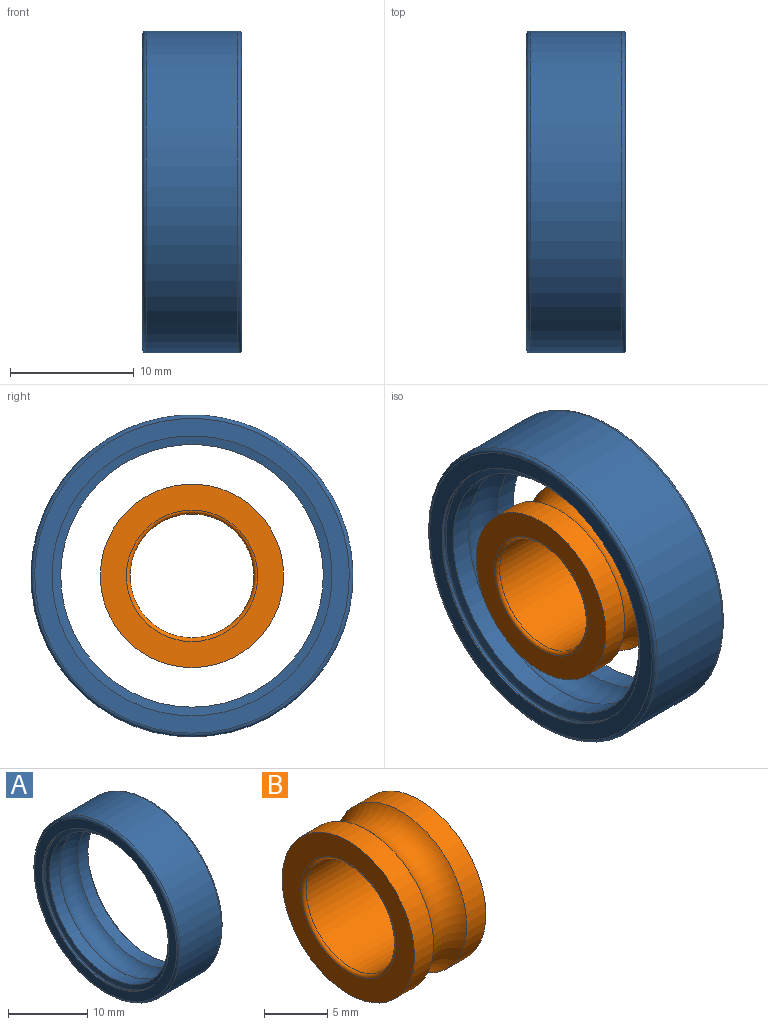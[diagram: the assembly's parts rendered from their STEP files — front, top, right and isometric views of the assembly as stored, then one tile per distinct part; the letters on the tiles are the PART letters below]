
ASSEMBLY  parts=2 mates=1
PART A: 14 faces, bbox 8x28.1x28.1 mm
  f0: plane 25.4x25.4mm, normal (-1,0,0), area 105.6mm2, adj f1,f13
  f1: cylinder r=11.3mm len=22.6mm, axis (-1,0,0), area 6.4mm2, adj f0,f2
  f2: torus R=11.3mm, axis (1,0,0), area 40.6mm2, adj f1,f3
  f3: cone r=11.3mm half-angle=80deg, axis (-1,0,0), area 48.9mm2, adj f2,f4
  f4: cylinder r=10.6mm len=21.2mm, axis (-1,0,0), area 117.2mm2, adj f3,f5
  f5: torus R=8.9mm, axis (1,0,0), area 256.4mm2, adj f4,f6
  f6: cylinder r=10.6mm len=21.2mm, axis (-1,0,0), area 117.2mm2, adj f5,f7
  f7: cone r=10.6mm half-angle=80deg, axis (1,0,0), area 48.9mm2, adj f6,f8
  f8: torus R=11.3mm, axis (1,0,0), area 40.6mm2, adj f7,f9
  f9: cylinder r=11.3mm len=22.6mm, axis (-1,0,0), area 6.4mm2, adj f8,f10
  f10: plane 25.4x25.4mm, normal (1,0,0), area 105.6mm2, adj f9,f11
  f11: torus R=12.7mm, axis (1,0,0), area 38.2mm2, adj f10,f12
  f12: cylinder r=13mm len=26mm, axis (-1,0,0), area 604.4mm2, adj f11,f13
  f13: torus R=12.7mm, axis (1,0,0), area 38.2mm2, adj f0,f12
PART B: 8 faces, bbox 8x19.3x19.3 mm
  f0: plane 14.8x14.8mm, normal (-1,0,0), area 83.8mm2, adj f1,f7
  f1: torus R=5.3mm, axis (1,0,0), area 15.1mm2, adj f0,f2
  f2: cylinder r=5mm len=10mm, axis (-1,0,0), area 232.5mm2, adj f1,f3
  f3: torus R=5.3mm, axis (1,0,0), area 15.1mm2, adj f2,f4
  f4: plane 14.8x14.8mm, normal (1,0,0), area 83.8mm2, adj f3,f5
  f5: cylinder r=7.4mm len=14.8mm, axis (-1,0,0), area 100mm2, adj f4,f6
  f6: torus R=8.9mm, axis (1,0,0), area 181.5mm2, adj f5,f7
  f7: cylinder r=7.4mm len=14.8mm, axis (-1,0,0), area 100mm2, adj f0,f6
PLACE A at identity
PLACE B at identity
MATE fastened B.f1 <-> A.f1  axis (1,0,0) through (8,0,0)mm
